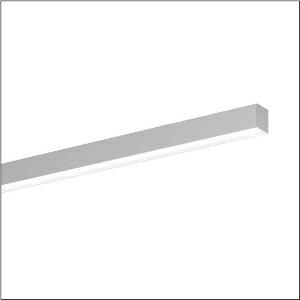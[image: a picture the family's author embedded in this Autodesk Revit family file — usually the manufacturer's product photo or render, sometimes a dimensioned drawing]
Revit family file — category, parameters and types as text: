
# Revit family: silica_r__21_51mx20da32sb_8410
name_source: partatom
category: Lighting Fixtures
units: mm (PartAtom-declared; Revit-internal decimal feet)

## family parameters
Cut with Voids When Loaded = No
Host = Face
Light Source = No
Part Type = Normal
Room Calculation Point = No
Round Connector Dimension = Use Diameter
Shared = No

## types (1)
- --- (1 x LED, 2400 lm, 16.1 W, 3000K)
    Apparent Load = 16 VA
    CIE Flux Codes = 48 79 96 100 100
    Color Rendering = 80
    Color Temperature = 3000K
    Default Elevation = 1800 mm
    Description = Silica® 21, office luminaire, primary optical cover: cover, of PMMA, opal, light emission: direct distribution, primary light characteristic: symmetric, installation type: surface-mounted, LED, rated luminous flux: 2.400lm, luminous efficacy: 149lm/W, light colour: 830, colour temperature: 3000K, with terminal, 3+2-pole, max. 2.5mm², mains connection: 220..240V, AC, 50/60Hz, rated input power: 16.1W, luminaire housing, of aluminium, metallic grey (RAL 9006), length: 1.204mm, width: 53mm, height: 53mm, protection rating (complete): IP20, insulation class (complete): insulation class I (protective earthing), certification: CE, permissible operating ambient temperature: 0..+35°C, standard: EN 50419, packaging unit: 1 piece
    Height = 0 mm  [stored 0 ft]
    Lamp = 1 x LED
    Lamp Light Flux = 2400 lm
    Lamp Power = 16.1 W
    Lamp count = 1
    Length = 1204 mm
    Luminous efficacy = 149 lm/W
    Manufacturer = Siteco
    ModVariant = No
    Model = 51MX20DA32SB
    Mounting Place = Ceiling
    Mounting Type = Recessed
    Number of Poles = 1
    OnlyDefault = Yes
    Power Factor = 1
    Product Name = Silica® 21
    Product group = office luminaire | ceiling recessed
    ProductGroupID = 400
    Protection Class = Protection class I
    Protection Degree = IP 20
    RLX_Detail_Level = 1
    RLX_Emergency_Light_Flux = 0 lm
    RLX_Emergency_Type = 0
    RLX_Emergency_Type_DB = No
    RlxData = <blob elided: 26333 chars, md5=89ed1d1d>
    Socket = socket
    Standby Power = 0 W
    System Light Flux = 2400 lm
    System Power = 16 W
    Type Comments = factory setting: luminous flux: 100 % | dim-lin: 254 | 233 mA
    Type Image = l_1335933.jpg
    URL = http://relux.com
    VarID = @adj_086977
    Voltage = 0 V
    Weight = 0.00 kg
    Width = 53 mm

note: [stored X ft] marks values corroborated as IEEE doubles in the binary element streams (Revit-internal decimal feet)

## geometry (parser evidence)
native form markers: Blend x4, Sweep x11
no freeform markers — native parametric forms only
